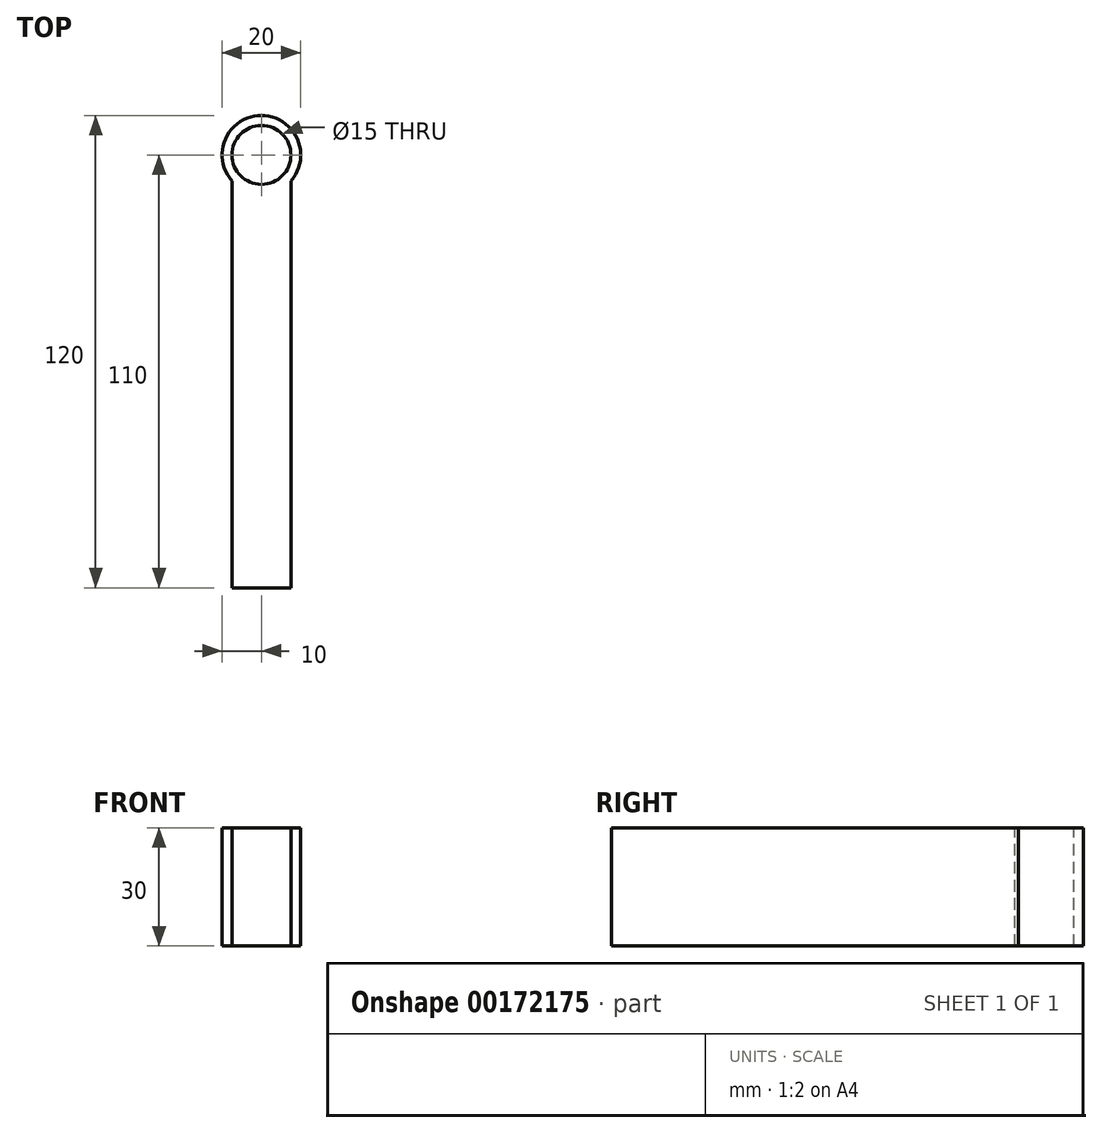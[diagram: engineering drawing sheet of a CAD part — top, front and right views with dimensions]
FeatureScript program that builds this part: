
annotation { "Feature Type Name" : "Feature", "Feature Type Description" : "" }
export const myFeature = defineFeature(function(context is Context, id is Id, definition is map)
    precondition{}
    {
        {
            var Q0;
            Q0=qCreatedBy(makeId("Top.planeOp"),FACE);
            var sketch = newSketch(context, id + "F0", { "sketchPlane" : qUnion([Q0])});
            skCircle(sketch, "E0", {"center": v(0, 0) * mm, "radius": 10 * mm});
            skSolve(sketch);
        }
        {
            var Q0;
            Q0 = qSketchRegion(id + "F0", true);
            extrude(context, id + "F1", {"entities" : qUnion([Q0]), "depth" : 30 * mm});
        }
        {
            var Q0;
            Q0=qCreatedBy(makeId("Front.planeOp"),FACE);
            var sketch = newSketch(context, id + "F2", { "sketchPlane" : qUnion([Q0])});
            skLineSegment(sketch, "E1.bottom", {"start": v(-7.5, 30) * mm, "end": v(7.5, 30) * mm});
            skLineSegment(sketch, "E1.top", {"start": v(-7.5, 0) * mm, "end": v(7.5, 0) * mm});
            skLineSegment(sketch, "E1.left", {"start": v(-7.5, 30) * mm, "end": v(-7.5, 0) * mm});
            skLineSegment(sketch, "E1.right", {"start": v(7.5, 30) * mm, "end": v(7.5, 0) * mm});
            skSolve(sketch);
        }
        {
            var Q0;
            Q0 = qSketchRegion(id + "F2", true);
            extrude(context, id + "F3", {"entities" : qUnion([Q0]), "operationType" : NewBodyOperationType.ADD, "depth" : 110 * mm});
        }
        {
            var Q0;
            Q0=makeQuery(id+"F3.boolean.opBoolean","MERGE",FACE,{"derivedFrom":[makeQuery(id+"F1.opExtrude","CAP_FACE",FACE,{"disambiguationData":[OSD([sQuery(id+"F0.wireOp",EDGE,"E0")])],"isStart":false}),makeQuery(id+"F3.opExtrude","SWEPT_FACE",FACE,{"disambiguationData":[OSD([sQuery(id+"F2.wireOp",EDGE,"E1.bottom")])]})]});
            var sketch = newSketch(context, id + "F4", { "sketchPlane" : qUnion([Q0])});
            skCircle(sketch, "E2", {"center": v(0, 0) * mm, "radius": 7.5 * mm});
            skSolve(sketch);
        }
        {
            var Q0;
            Q0 = qSketchRegion(id + "F4", true);
            extrude(context, id + "F5", {"entities" : qUnion([Q0]), "operationType" : NewBodyOperationType.REMOVE, "endBound" : BoundingType.UP_TO_NEXT, "oppositeDirection" : true, "depth" : 25 * mm});
        }
    });
